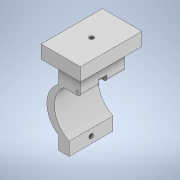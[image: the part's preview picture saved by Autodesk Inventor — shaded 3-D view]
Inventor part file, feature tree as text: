
AUTODESK INVENTOR PART (.ipt)
format: ipt  version: 2021 (Build 250183000, 183)  size: 183,296 bytes
history: native  units: in
note: dims shown in document units (in); Inventor stores cm internally (conversion verified against a paired STEP export)
features: sketch x6, extrude x5, hole x2, fillet x1
ambient origin geometry x8: Origin, YZ Plane, XZ Plane, XY Plane, X Axis, Y Axis, Z Axis, Center Point
bodies: Solid1 (feature_tree)
feature tree (14):
  extrude  "Extrusion1"  Depth=3.937in TaperAngle=0.0deg
  extrude  "Extrusion6"  Depth=3.937in
  extrude  "Extrusion7"  Depth=2.3622in
  hole  "Hole3"  [1 undecoded]
  extrude  "Extrusion8"  Depth=3.937in
  extrude  "Extrusion9"  Depth=5.5118in
  hole  "Hole4"  [1 undecoded]
  fillet  "Fillet1"  Radius=1.1811in
  sketch  "Sketch2"  dims[d1=1.9685in d2=3.937in d3=0.0in]
  sketch  "Sketch12"  dims[d55=0.9449in d56=3.937in]
  sketch  "Sketch13"  dims[d57=1.9685in d58=2.3622in]
  sketch  "Sketch16"  dims[d59=1.1811in d61=0.4724in]
  sketch  "Sketch18"  dims[d62=3.937in d63=0.0in d68=0.9843in]
  sketch  "Sketch19"  dims[d69=1.9685in d70=5.5118in d71=3.5433in d72=1.1811in d73=0.0in d74=0.3937in d75=0.315in d76=0.2362in d77=0.3937in d78=0.1181in d79=90.0deg d80=3.1496in d81=0.8108in d82=0.2756in d83=0.2756in d84=0.2756in d85=3.937in d86=0.0in d89=0.5118in d90=0.0in d91=0.5906in d92=0.3937in d93=0.3937in d94=0.2362in d95=0.3937in d96=0.1181in d97=90.0deg d98=0.315in d99=0.8108in d102=0.2362in d103=2.3622in d104=0.5512in d105=0.3937in d106=0.3937in d64=0.0197in d65=0.0344in d66=0.0197in d67=0.0344in]
note: 2 required parameter values undecoded (feature->parameter linkage not recoverable at this tier; creation-order binding heuristic only, values carry confidence <= 0.55)
